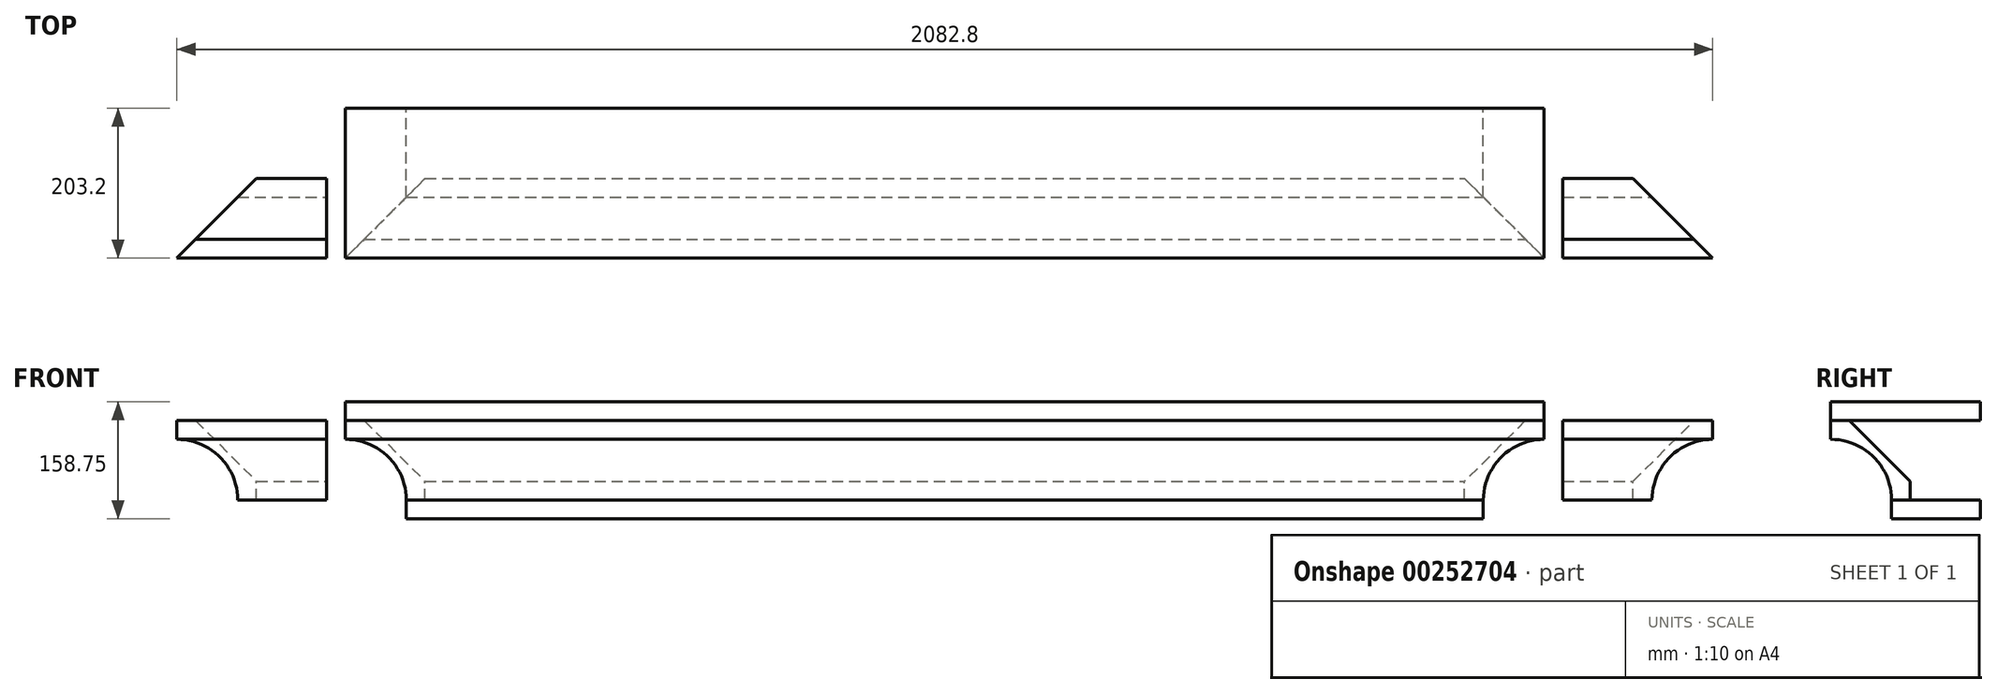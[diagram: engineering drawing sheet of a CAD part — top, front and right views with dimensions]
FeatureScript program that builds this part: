
annotation { "Feature Type Name" : "Feature", "Feature Type Description" : "" }
export const myFeature = defineFeature(function(context is Context, id is Id, definition is map)
    precondition{}
    {
        {
            var Q0;
            Q0=qCreatedBy(makeId("Right.planeOp"),FACE);
            var sketch = newSketch(context, id + "F0", { "sketchPlane" : qUnion([Q0])});
            skLineSegment(sketch, "E0", {"start": v(0, 0) * mm, "end": v(0, 25.4) * mm});
            skLineSegment(sketch, "E1", {"start": v(0, 25.4) * mm, "end": v(-82.55, 107.95) * mm});
            skLineSegment(sketch, "E2", {"start": v(-82.55, 107.95) * mm, "end": v(-107.95, 107.95) * mm});
            skLineSegment(sketch, "E3", {"start": v(-107.95, 107.95) * mm, "end": v(-107.95, 82.55) * mm});
            skLineSegment(sketch, "E4", {"start": v(-107.95, 82.55) * mm, "end": v(-107.95, 82.55) * mm});
            skLineSegment(sketch, "E5", {"start": v(-25.4, 0) * mm, "end": v(0, 0) * mm});
            skArc(sketch, "E6", {"start": v(-107.95, 82.55) * mm, "mid": v(-49.58, 58.37) * mm, "end": v(-25.4, 0) * mm});
            skSolve(sketch);
        }
        {
            var Q0;
            Q0 = qSketchRegion(id + "F0", true);
            extrude(context, id + "F1", {"entities" : qUnion([Q0]), "endBound" : BoundingType.SYMMETRIC, "oppositeDirection" : true, "depth" : 2082.8 * mm});
        }
        {
            var Q0;
            Q0=makeQuery(id+"F1.opExtrude","SWEPT_FACE",FACE,{"disambiguationData":[OSD([sQuery(id+"F0.wireOp",EDGE,"E2")])]});
            var sketch = newSketch(context, id + "F2", { "sketchPlane" : qUnion([Q0])});
            skLineSegment(sketch, "E7", {"start": v(-1041.4, -107.95) * mm, "end": v(-933.45, 0) * mm});
            skLineSegment(sketch, "E8", {"start": v(-933.45, 0) * mm, "end": v(-1041.4, 0) * mm});
            skLineSegment(sketch, "E9", {"start": v(-1041.4, 0) * mm, "end": v(-1041.4, -107.95) * mm});
            skLineSegment(sketch, "E10", {"start": v(1041.4, -107.95) * mm, "end": v(1041.4, 0) * mm});
            skLineSegment(sketch, "E11", {"start": v(1041.4, 0) * mm, "end": v(933.45, 0) * mm});
            skLineSegment(sketch, "E12", {"start": v(933.45, 0) * mm, "end": v(1041.4, -107.95) * mm});
            skLineSegment(sketch, "E13", {"start": v(-838.2, 0) * mm, "end": v(-838.2, -107.95) * mm});
            skLineSegment(sketch, "E14", {"start": v(-838.2, -107.95) * mm, "end": v(-812.8, -107.95) * mm});
            skLineSegment(sketch, "E15", {"start": v(-812.8, -107.95) * mm, "end": v(-704.85, 0) * mm});
            skLineSegment(sketch, "E16", {"start": v(-704.85, 0) * mm, "end": v(-838.2, 0) * mm});
            skLineSegment(sketch, "E17", {"start": v(838.2, 0) * mm, "end": v(838.2, -107.95) * mm});
            skLineSegment(sketch, "E18", {"start": v(838.2, -107.95) * mm, "end": v(812.8, -107.95) * mm});
            skLineSegment(sketch, "E19", {"start": v(812.8, -107.95) * mm, "end": v(704.85, 0) * mm});
            skLineSegment(sketch, "E20", {"start": v(704.85, 0) * mm, "end": v(838.2, 0) * mm});
            skSolve(sketch);
        }
        {
            var Q0;
            Q0 = qSketchRegion(id + "F2", true);
            extrude(context, id + "F3", {"entities" : qUnion([Q0]), "operationType" : NewBodyOperationType.REMOVE, "endBound" : BoundingType.THROUGH_ALL, "oppositeDirection" : true, "depth" : 25.4 * mm});
        }
        {
            var Q0;
            Q0=makeQuery(id+"F3.boolean.opBoolean","SPLIT",FACE,{"disambiguationData":[TD([makeQuery(id+"F3.opExtrude","SWEPT_FACE",FACE,{"disambiguationData":[OSD([sQuery(id+"F2.wireOp",EDGE,"E15")])]})])],"derivedFrom":makeQuery(id+"F1.opExtrude","SWEPT_FACE",FACE,{"disambiguationData":[OSD([sQuery(id+"F0.wireOp",EDGE,"E5")])]})});
            var sketch = newSketch(context, id + "F4", { "sketchPlane" : qUnion([Q0])});
            skLineSegment(sketch, "E21.bottom", {"start": v(-730.25, 25.4) * mm, "end": v(730.25, 25.4) * mm});
            skLineSegment(sketch, "E21.top", {"start": v(-730.25, -95.25) * mm, "end": v(730.25, -95.25) * mm});
            skLineSegment(sketch, "E21.left", {"start": v(-730.25, 25.4) * mm, "end": v(-730.25, -95.25) * mm});
            skLineSegment(sketch, "E21.right", {"start": v(730.25, 25.4) * mm, "end": v(730.25, -95.25) * mm});
            skSolve(sketch);
        }
        {
            var Q0;
            Q0 = qSketchRegion(id + "F4", true);
            extrude(context, id + "F5", {"entities" : qUnion([Q0]), "depth" : 25.4 * mm});
        }
        {
            var Q0;
            Q0=makeQuery(id+"F3.boolean.opBoolean","SPLIT",FACE,{"disambiguationData":[TD([makeQuery(id+"F3.opExtrude","SWEPT_FACE",FACE,{"disambiguationData":[OSD([sQuery(id+"F2.wireOp",EDGE,"E15")])]})])],"derivedFrom":makeQuery(id+"F1.opExtrude","SWEPT_FACE",FACE,{"disambiguationData":[OSD([sQuery(id+"F0.wireOp",EDGE,"E2")])]})});
            var sketch = newSketch(context, id + "F6", { "sketchPlane" : qUnion([Q0])});
            skLineSegment(sketch, "E22.bottom", {"start": v(-812.8, -107.95) * mm, "end": v(812.8, -107.95) * mm});
            skLineSegment(sketch, "E22.top", {"start": v(-812.8, 95.25) * mm, "end": v(812.8, 95.25) * mm});
            skLineSegment(sketch, "E22.left", {"start": v(-812.8, 95.25) * mm, "end": v(-812.8, -107.95) * mm});
            skLineSegment(sketch, "E22.right", {"start": v(812.8, 95.25) * mm, "end": v(812.8, -107.95) * mm});
            skSolve(sketch);
        }
        {
            var Q0;
            Q0 = qSketchRegion(id + "F6", true);
            extrude(context, id + "F7", {"entities" : qUnion([Q0]), "depth" : 25.4 * mm});
        }
    });
